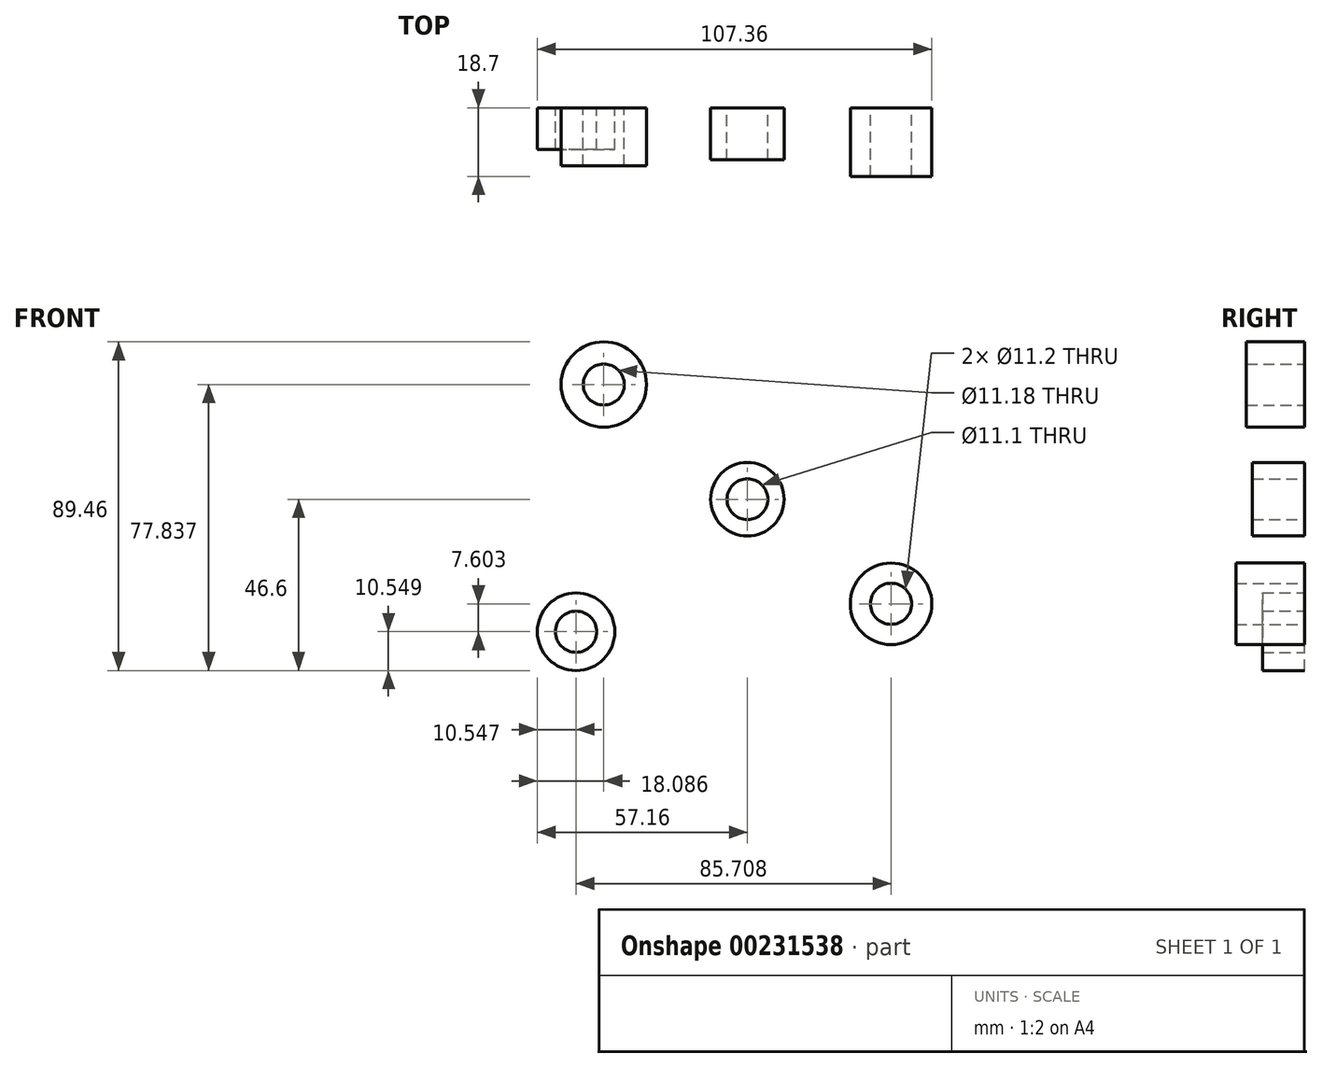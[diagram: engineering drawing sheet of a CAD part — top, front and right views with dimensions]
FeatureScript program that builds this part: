
annotation { "Feature Type Name" : "Feature", "Feature Type Description" : "" }
export const myFeature = defineFeature(function(context is Context, id is Id, definition is map)
    precondition{}
    {
        {
            var Q0;
            Q0=qCreatedBy(makeId("Front.planeOp"),FACE);
            var sketch = newSketch(context, id + "F0", { "sketchPlane" : qUnion([Q0])});
            skCircle(sketch, "E0", {"center": v(0, 0) * mm, "radius": 5.55 * mm});
            skCircle(sketch, "E1", {"center": v(0, 0) * mm, "radius": 10 * mm});
            skSolve(sketch);
        }
        {
            var Q0;
            Q0=makeQuery(id+"F0.imprint","IMPRINT",FACE,{"disambiguationData":[TD([[makeQuery(id+"F0.imprint","IMPRINT",EDGE,{"derivedFrom":sQuery(id+"F0.wireOp",EDGE,"E0")}),-1.0]])]});
            extrude(context, id + "F1", {"entities" : qUnion([Q0]), "depth" : 14.2 * mm});
        }
        {
            var Q0;
            Q0=qCreatedBy(makeId("Front.planeOp"),FACE);
            var sketch = newSketch(context, id + "F2", { "sketchPlane" : qUnion([Q0])});
            skCircle(sketch, "E2", {"center": v(39.71, 31.24) * mm, "radius": 5.6 * mm});
            skCircle(sketch, "E3", {"center": v(39.71, 31.24) * mm, "radius": 11.1 * mm});
            skCircle(sketch, "E4", {"center": v(-39.07, 31.24) * mm, "radius": 5.6 * mm});
            skCircle(sketch, "E5", {"center": v(-39.07, 31.24) * mm, "radius": 11.62 * mm});
            skCircle(sketch, "E6", {"center": v(-38.5, -27) * mm, "radius": 5.6 * mm});
            skCircle(sketch, "E7", {"center": v(-38.5, -27) * mm, "radius": 10.55 * mm});
            skSolve(sketch);
        }
        {
            var Q0;
            Q0=makeQuery(id+"F2.imprint","IMPRINT",FACE,{"disambiguationData":[TD([[makeQuery(id+"F2.imprint","IMPRINT",EDGE,{"derivedFrom":sQuery(id+"F2.wireOp",EDGE,"E4")}),-1.0]])]});
            extrude(context, id + "F3", {"entities" : qUnion([Q0]), "depth" : 15.8 * mm});
        }
        {
            var Q0;
            Q0=qCreatedBy(makeId("Front.planeOp"),FACE);
            var sketch = newSketch(context, id + "F4", { "sketchPlane" : qUnion([Q0])});
            skCircle(sketch, "E8", {"center": v(-46.61, -36.05) * mm, "radius": 5.6 * mm});
            skCircle(sketch, "E9", {"center": v(-46.61, -36.05) * mm, "radius": 10.55 * mm});
            skSolve(sketch);
        }
        {
            var Q0;
            Q0=makeQuery(id+"F4.imprint","IMPRINT",FACE,{"disambiguationData":[TD([[makeQuery(id+"F4.imprint","IMPRINT",EDGE,{"derivedFrom":sQuery(id+"F4.wireOp",EDGE,"E8")}),-1.0]])]});
            var Q1;
            Q1=sQuery(id+"F4.wireOp",EDGE,"E9");
            var Q2;
            Q2=sQuery(id+"F4.wireOp",EDGE,"E8");
            extrude(context, id + "F5", {"entities" : qUnion([Q0]), "surfaceEntities" : qUnion([Q1, Q2]), "depth" : 11.4 * mm});
        }
        {
            var Q0;
            Q0=qCreatedBy(makeId("Front.planeOp"),FACE);
            var sketch = newSketch(context, id + "F6", { "sketchPlane" : qUnion([Q0])});
            skCircle(sketch, "E10", {"center": v(39.1, -28.45) * mm, "radius": 5.6 * mm});
            skCircle(sketch, "E11", {"center": v(39.1, -28.45) * mm, "radius": 11.1 * mm});
            skSolve(sketch);
        }
        {
            var Q0;
            Q0=makeQuery(id+"F6.imprint","IMPRINT",FACE,{"disambiguationData":[TD([[makeQuery(id+"F6.imprint","IMPRINT",EDGE,{"derivedFrom":sQuery(id+"F6.wireOp",EDGE,"E10")}),-1.0]])]});
            var Q1;
            Q1=sQuery(id+"F6.wireOp",EDGE,"E10");
            var Q2;
            Q2=sQuery(id+"F6.wireOp",EDGE,"E11");
            extrude(context, id + "F7", {"entities" : qUnion([Q0]), "surfaceEntities" : qUnion([Q1, Q2]), "depth" : 18.7 * mm});
        }
    });
